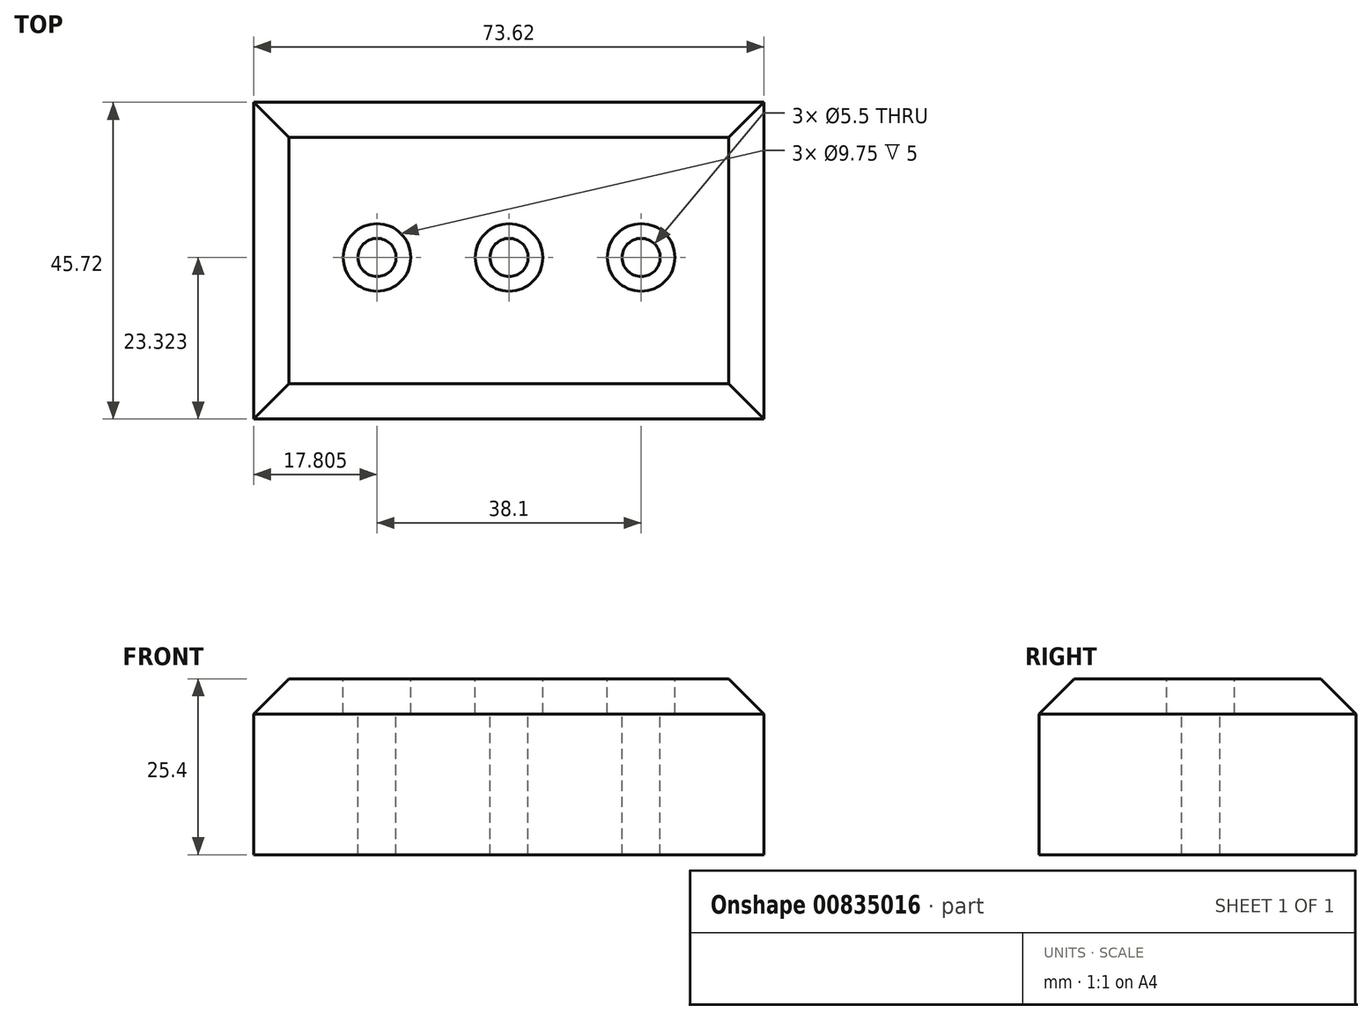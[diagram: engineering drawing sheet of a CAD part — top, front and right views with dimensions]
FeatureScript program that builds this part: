
annotation { "Feature Type Name" : "Feature", "Feature Type Description" : "" }
export const myFeature = defineFeature(function(context is Context, id is Id, definition is map)
    precondition{}
    {
        {
            var Q0;
            Q0=qCreatedBy(makeId("Top.planeOp"),FACE);
            var sketch = newSketch(context, id + "F0", { "sketchPlane" : qUnion([Q0])});
            skLineSegment(sketch, "E0.bottom", {"start": v(36.8, 22.86) * mm, "end": v(-36.8, 22.86) * mm});
            skLineSegment(sketch, "E0.top", {"start": v(36.8, -22.86) * mm, "end": v(-36.8, -22.86) * mm});
            skLineSegment(sketch, "E0.left", {"start": v(36.8, 22.86) * mm, "end": v(36.8, -22.86) * mm});
            skLineSegment(sketch, "E0.right", {"start": v(-36.8, 22.86) * mm, "end": v(-36.8, -22.86) * mm});
            skPoint(sketch, "E0.middle", {"position": v(0, 0) * mm});
            skSolve(sketch);
        }
        {
            var Q0;
            Q0 = qSketchRegion(id + "F0", true);
            extrude(context, id + "F1", {"entities" : qUnion([Q0]), "depth" : 25.4 * mm, "offsetDistance" : 25.4 * mm});
        }
        {
            var Q0;
            Q0=makeQuery(id+"F1.opExtrude","CAP_FACE",FACE,{"disambiguationData":[OSD([sQuery(id+"F0.wireOp",EDGE,"E0.bottom"),sQuery(id+"F0.wireOp",EDGE,"E0.top"),sQuery(id+"F0.wireOp",EDGE,"E0.left"),sQuery(id+"F0.wireOp",EDGE,"E0.right")])],"isStart":false});
            var sketch = newSketch(context, id + "F2", { "sketchPlane" : qUnion([Q0])});
            skPoint(sketch, "E1", {"position": v(0.05, 0.46) * mm});
            skPoint(sketch, "E2", {"position": v(3.67, 22.86) * mm});
            skPoint(sketch, "E3", {"position": v(19.1, 0.46) * mm});
            skPoint(sketch, "E4", {"position": v(-19, 0.46) * mm});
            skSolve(sketch);
        }
        {
            var Q0;
            Q0=sQuery(id+"F2.wireOp",VERTEX,"E1");
            var Q1;
            Q1=sQuery(id+"F2.wireOp",VERTEX,"E4");
            var Q2;
            Q2=sQuery(id+"F2.wireOp",VERTEX,"E3");
            var Q3;
            Q3=makeQuery(id+"F1.opExtrude","SWEPT_BODY",BODY,{"disambiguationData":[OSD([sQuery(id+"F0.wireOp",EDGE,"E0.bottom"),sQuery(id+"F0.wireOp",EDGE,"E0.top"),sQuery(id+"F0.wireOp",EDGE,"E0.left"),sQuery(id+"F0.wireOp",EDGE,"E0.right")])]});
            hole(context, id + "F3", {"style" : HoleStyle.C_BORE, "endStyle" : HoleEndStyle.THROUGH, "standardTappedOrClearance" : lookupTablePath({ "standard" : "ISO", "fit" : "Normal", "size" : "M5", "type" : "Clearance" }), "standardBlindInLast" : lookupTablePath({ "fit" : "Standard", "standard" : "ISO", "size" : "M5", "type" : "Clearance" }), "holeDiameter" : 5.5 * mm, "cBoreDiameter" : 9.75 * mm, "cBoreDepth" : 5 * mm, "majorDiameter" : 6.35 * mm, "isTappedThrough" : true, "tappedDepth" : 12.7 * mm, "tapClearance" : 3, "locations" : qUnion([Q0, Q1, Q2]), "scope" : qUnion([Q3])});
        }
        {
            var Q0;
            Q0=makeQuery(id+"F1.opExtrude","CAP_EDGE",EDGE,{"disambiguationData":[OSD([sQuery(id+"F0.wireOp",EDGE,"E0.left")])],"isStart":false});
            var Q1;
            Q1=makeQuery(id+"F1.opExtrude","CAP_EDGE",EDGE,{"disambiguationData":[OSD([sQuery(id+"F0.wireOp",EDGE,"E0.bottom")])],"isStart":false});
            var Q2;
            Q2=makeQuery(id+"F1.opExtrude","CAP_EDGE",EDGE,{"disambiguationData":[OSD([sQuery(id+"F0.wireOp",EDGE,"E0.right")])],"isStart":false});
            var Q3;
            Q3=makeQuery(id+"F1.opExtrude","CAP_EDGE",EDGE,{"disambiguationData":[OSD([sQuery(id+"F0.wireOp",EDGE,"E0.top")])],"isStart":false});
            chamfer(context, id + "F4", {"entities" : qUnion([Q0, Q1, Q2, Q3]), "width" : 5.08 * mm, "tangentPropagation" : true});
        }
    });
